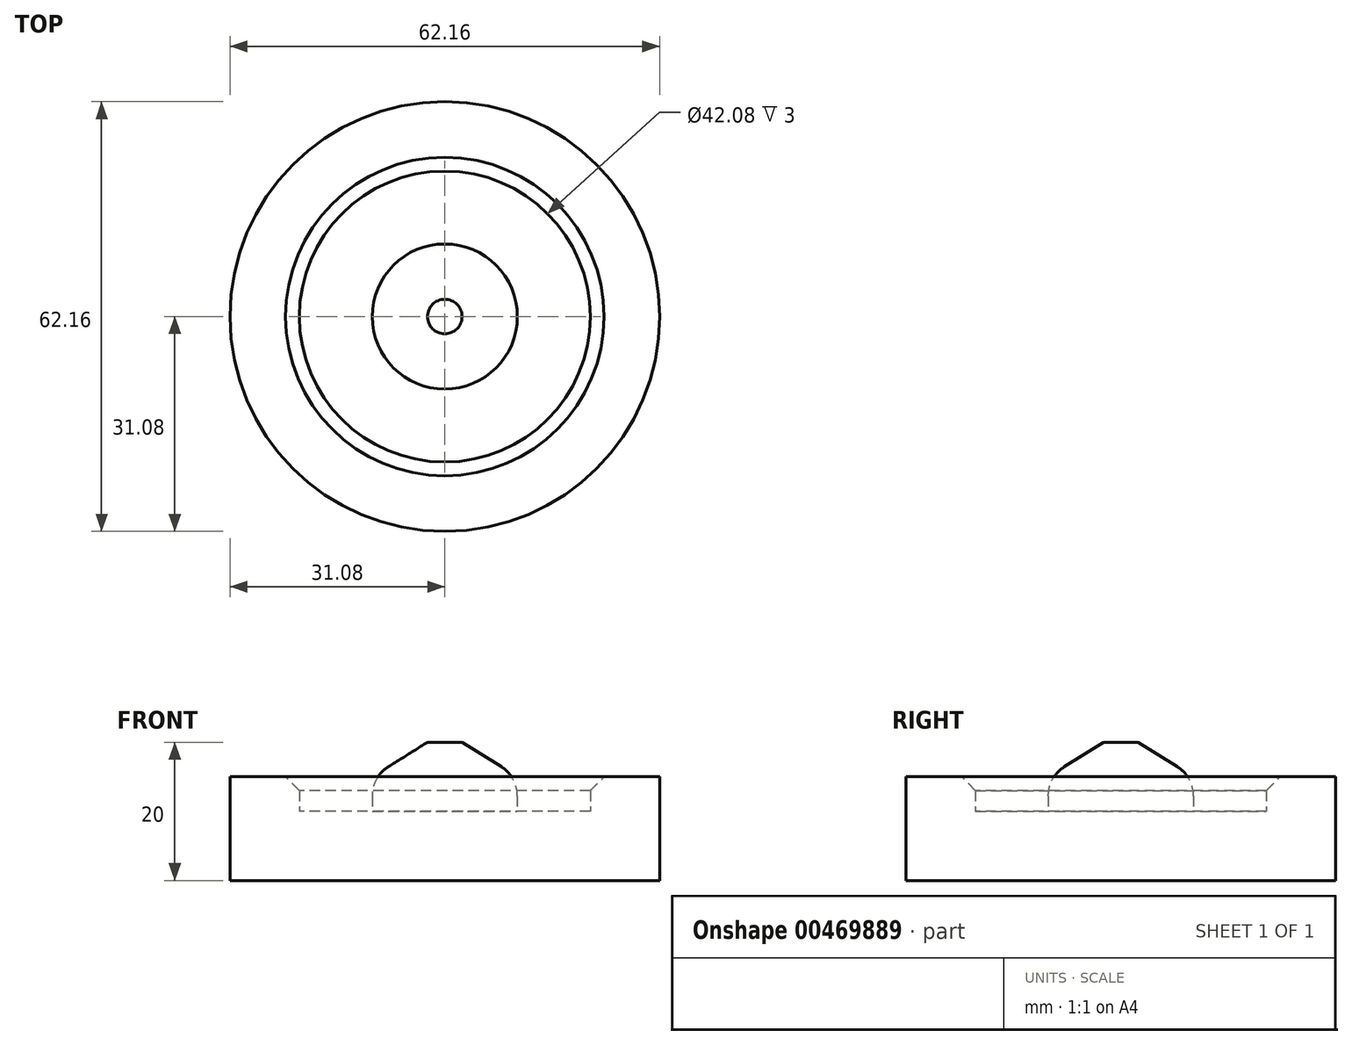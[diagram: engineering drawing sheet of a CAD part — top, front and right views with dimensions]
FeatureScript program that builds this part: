
annotation { "Feature Type Name" : "Feature", "Feature Type Description" : "" }
export const myFeature = defineFeature(function(context is Context, id is Id, definition is map)
    precondition{}
    {
        {
            var Q0;
            Q0=qCreatedBy(makeId("Top.planeOp"),FACE);
            var sketch = newSketch(context, id + "F0", { "sketchPlane" : qUnion([Q0])});
            skCircle(sketch, "E0", {"center": v(0, 0) * mm, "radius": 31.08 * mm});
            skCircle(sketch, "E1", {"center": v(0, 0) * mm, "radius": 21.04 * mm});
            skCircle(sketch, "E2", {"center": v(0, 0) * mm, "radius": 10.5 * mm});
            skSolve(sketch);
        }
        {
            var Q0;
            Q0=makeQuery(id+"F0.imprint","IMPRINT",FACE,{"disambiguationData":[TD([[makeQuery(id+"F0.imprint","IMPRINT",EDGE,{"derivedFrom":sQuery(id+"F0.wireOp",EDGE,"E2")}),1.0]])]});
            extrude(context, id + "F1", {"entities" : qUnion([Q0]), "depth" : 15 * mm, "offsetDistance" : 25 * mm});
        }
        {
            var Q0;
            Q0=qCreatedBy(makeId("Front.planeOp"),FACE);
            var sketch = newSketch(context, id + "F2", { "sketchPlane" : qUnion([Q0])});
            skLineSegment(sketch, "E3", {"start": v(10.5, 15) * mm, "end": v(0, 15) * mm});
            skLineSegment(sketch, "E4", {"start": v(0, 15) * mm, "end": v(0, 20) * mm});
            skLineSegment(sketch, "E5", {"start": v(10.5, 15) * mm, "end": v(2.5, 20) * mm});
            skLineSegment(sketch, "E6", {"start": v(2.5, 20) * mm, "end": v(0, 20) * mm});
            skSolve(sketch);
        }
        {
            var Q0;
            Q0=makeQuery(id+"F2.imprint","IMPRINT",FACE,{"disambiguationData":[TD([[makeQuery(id+"F2.imprint","IMPRINT",EDGE,{"derivedFrom":sQuery(id+"F2.wireOp",EDGE,"E3")}),-1.0]])]});
            var Q1;
            Q1=sQuery(id+"F2.wireOp",EDGE,"E4");
            revolve(context, id + "F3", {"operationType" : NewBodyOperationType.ADD, "entities" : qUnion([Q0]), "axis" : qUnion([Q1]), "revolveType" : RevolveType.FULL});
        }
        {
            var Q0;
            Q0=makeQuery(id+"F0.imprint","IMPRINT",FACE,{"disambiguationData":[TD([[makeQuery(id+"F0.imprint","IMPRINT",EDGE,{"derivedFrom":sQuery(id+"F0.wireOp",EDGE,"E1")}),1.0]])]});
            extrude(context, id + "F4", {"entities" : qUnion([Q0]), "operationType" : NewBodyOperationType.ADD, "depth" : 10 * mm, "offsetDistance" : 25 * mm});
        }
        {
            var Q0;
            Q0=makeQuery(id+"F0.imprint","IMPRINT",FACE,{"disambiguationData":[TD([[makeQuery(id+"F0.imprint","IMPRINT",EDGE,{"derivedFrom":sQuery(id+"F0.wireOp",EDGE,"E0")}),1.0]])]});
            extrude(context, id + "F5", {"entities" : qUnion([Q0]), "operationType" : NewBodyOperationType.ADD, "depth" : 15 * mm, "offsetDistance" : 25 * mm});
        }
        {
            var Q0;
            Q0=makeQuery(id+"F5.opExtrude","CAP_EDGE",EDGE,{"disambiguationData":[OSD([sQuery(id+"F0.wireOp",EDGE,"E1")])],"isStart":false});
            chamfer(context, id + "F6", {"entities" : qUnion([Q0]), "width" : 2 * mm, "tangentPropagation" : true});
        }
        {
            var Q0;
            Q0=makeQuery(id+"F3.boolean.opBoolean","MERGE",EDGE,{"derivedFrom":[makeQuery(id+"F1.opExtrude","CAP_EDGE",EDGE,{"disambiguationData":[OSD([sQuery(id+"F0.wireOp",EDGE,"E2")])],"isStart":false}),makeQuery(id+"F3.opRevolve","SWEPT_EDGE",EDGE,{"disambiguationData":[OSD([sQuery(id+"F2.wireOp",EDGE,"dc7Y9k7k-4YDQ-OFhQ-Bwd1-31yhVCNW8iLt"),sQuery(id+"F2.wireOp",EDGE,"E3")])]})]});
            fillet(context, id + "F7", {"entities" : qUnion([Q0]), "radius" : 5 * mm, "tangentPropagation" : true, "allowEdgeOverflow" : false});
        }
    });
